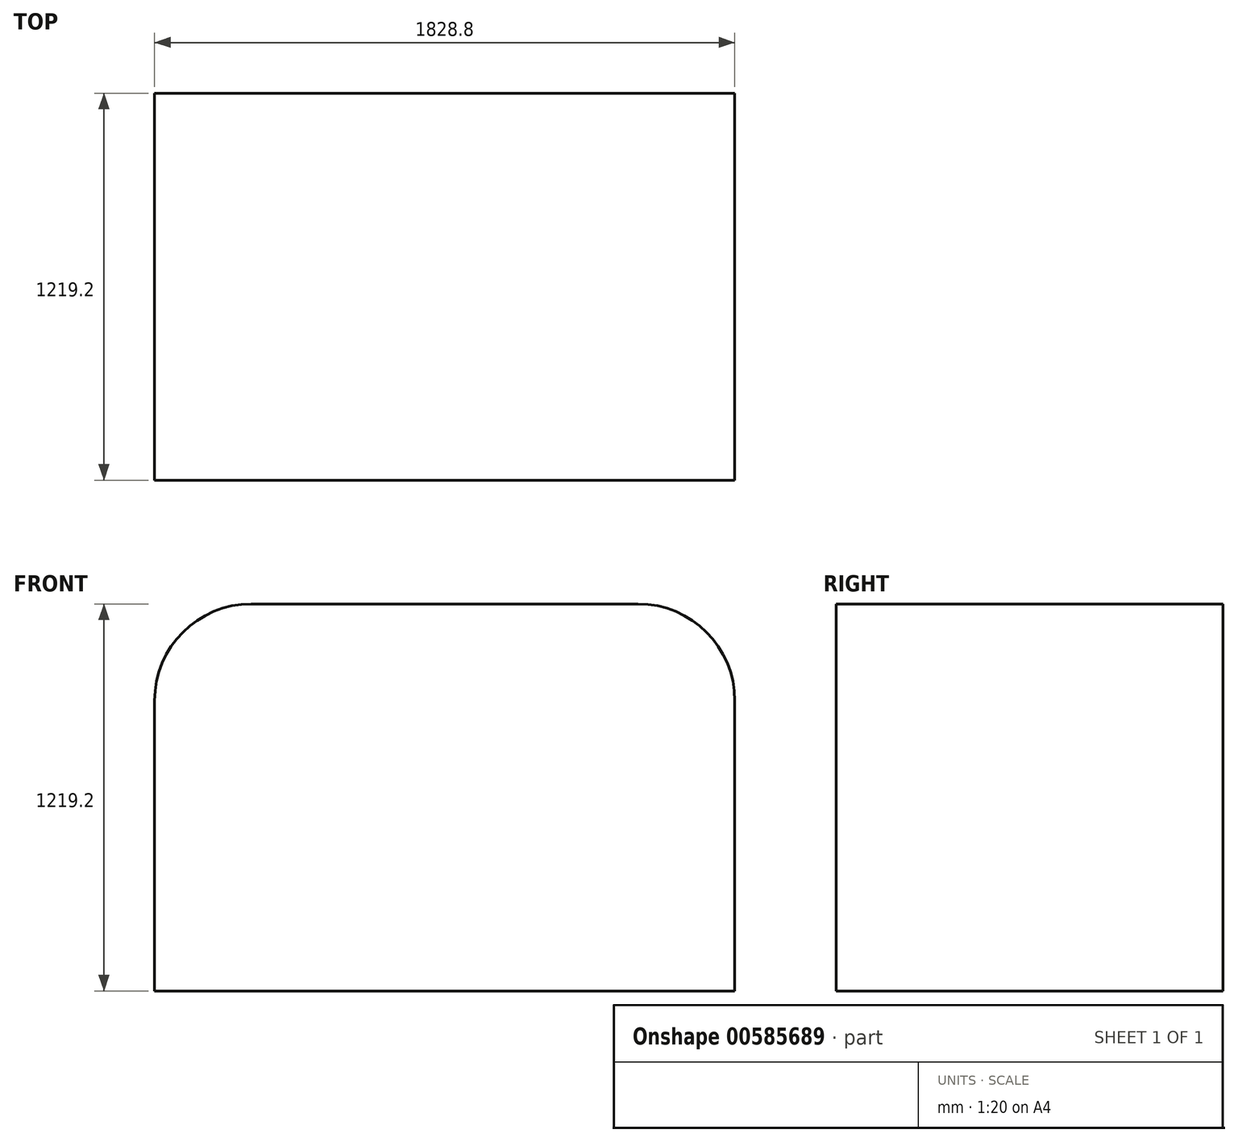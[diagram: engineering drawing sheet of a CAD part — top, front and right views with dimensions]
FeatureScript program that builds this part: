
annotation { "Feature Type Name" : "Feature", "Feature Type Description" : "" }
export const myFeature = defineFeature(function(context is Context, id is Id, definition is map)
    precondition{}
    {
        {
            var Q0;
            Q0=qCreatedBy(makeId("Front.planeOp"),FACE);
            var sketch = newSketch(context, id + "F0", { "sketchPlane" : qUnion([Q0])});
            skLineSegment(sketch, "E0.bottom", {"start": v(0, 0) * mm, "end": v(-1828.8, 0) * mm});
            skLineSegment(sketch, "E0.top", {"start": v(-304.8, 1219.2) * mm, "end": v(-1524, 1219.2) * mm});
            skLineSegment(sketch, "E0.left", {"start": v(0, 0) * mm, "end": v(0, 914.4) * mm});
            skLineSegment(sketch, "E0.right", {"start": v(-1828.8, 0) * mm, "end": v(-1828.8, 914.4) * mm});
            skPoint(sketch, "E1.visualSharp", {"position": v(-1828.8, 1219.2) * mm});
            skArc(sketch, "E1.filletArc", {"start": v(-1524, 1219.2) * mm, "mid": v(-1739.53, 1129.93) * mm, "end": v(-1828.8, 914.4) * mm});
            skPoint(sketch, "E2.visualSharp", {"position": v(0, 1219.2) * mm});
            skArc(sketch, "E2.filletArc", {"start": v(0, 914.4) * mm, "mid": v(-89.27, 1129.93) * mm, "end": v(-304.8, 1219.2) * mm});
            skSolve(sketch);
        }
        {
            var Q0;
            Q0 = qSketchRegion(id + "F0", true);
            extrude(context, id + "F1", {"entities" : qUnion([Q0]), "depth" : 1219.2 * mm, "offsetDistance" : 25.4 * mm});
        }
    });
